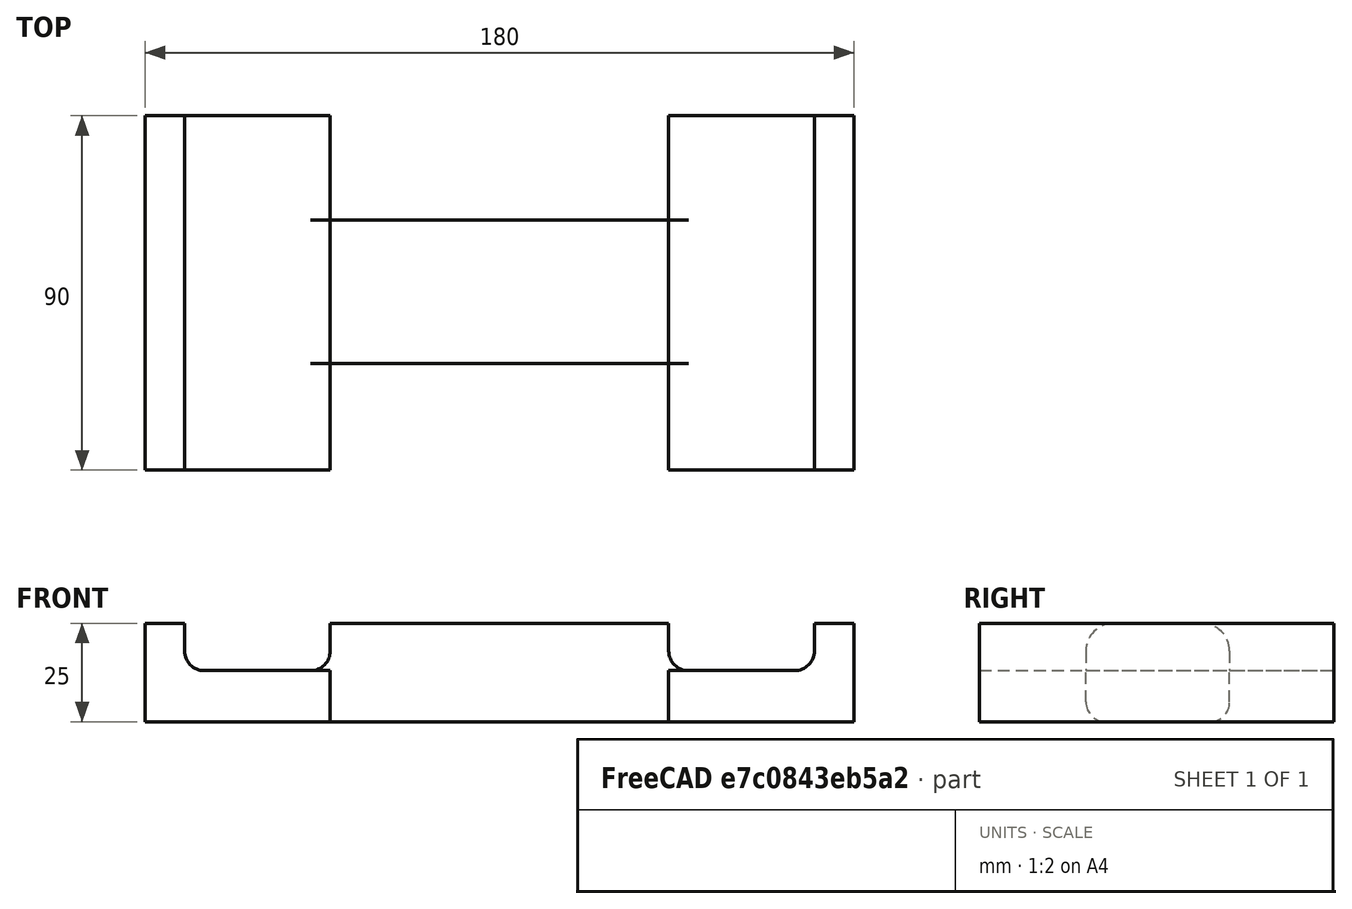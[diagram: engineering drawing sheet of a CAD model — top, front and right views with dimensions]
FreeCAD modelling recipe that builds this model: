
FCSTD DOCUMENT  (FreeCAD 0.19R24291 (Git))
Label: Drill-handle
License: Other
LicenseURL: https://www.gnu.org/licenses/gpl-3.0.en.html
objects: Part::Box×5, Part::Fillet×3, Part::MultiFuse×1, Part::Cut×1
note: 10 computed .brp shape members not serialized (recipe doc carries the construction recipe); baked Part::Feature solids carry a one-line shape summary decoded from their .brp

FEATURE [Part::Box] Box  label="Cube"
  AttacherType = Attacher::AttachEngine3D
  Height = 25
  Length = 180
  Width = 90
FEATURE [Part::Box] Box001  label="Cube001"
  AttacherType = Attacher::AttachEngine3D
  Height = 30
  Length = 37
  Placement = pos=(10,-5,13) rot=(0,0,1;0rad)
  Width = 100
FEATURE [Part::Box] Box002  label="Cube002"
  AttacherType = Attacher::AttachEngine3D
  Height = 30
  Length = 37
  Placement = pos=(133,-5,13) rot=(0,0,1;0rad)
  Width = 100
FEATURE [Part::Box] Box003  label="Cube003"
  AttacherType = Attacher::AttachEngine3D
  Height = 42
  Length = 86
  Placement = pos=(47,-1,-1) rot=(0,0,1;0rad)
  Width = 28
FEATURE [Part::Box] Box004  label="Cube004"
  AttacherType = Attacher::AttachEngine3D
  Height = 42
  Length = 86
  Placement = pos=(47,63.5,-1) rot=(0,0,1;0rad)
  Width = 27.5
FEATURE [Part::MultiFuse] Fusion
  Shapes = -> [Box001,Box002,Box003,Box004]
FEATURE [Part::Cut] Cut
  Base = -> Box
  Tool = -> Fusion
FEATURE [Part::Fillet] Fillet
  Base = -> Cut
  Edges = 4 edges r=5: [Edge27,Edge29,Edge53,Edge55]
FEATURE [Part::Fillet] Fillet001
  Base = -> Fillet
  Edges = 2 edges r=5: [Edge23,Edge29]
FEATURE [Part::Fillet] Fillet002
  Base = -> Fillet001
  Edges = 2 edges r=7: [Edge12,Edge56]
